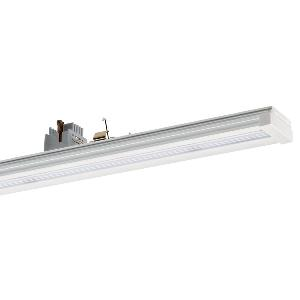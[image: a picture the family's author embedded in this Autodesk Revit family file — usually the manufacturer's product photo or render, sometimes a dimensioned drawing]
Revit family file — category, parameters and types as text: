
# Revit family: conveo_-_cvg_4500_840_w-p_ea_5_226848079-00804943_2f42
name_source: partatom
category: Lighting Fixtures
units: mm (PartAtom-declared; Revit-internal decimal feet)

## family parameters
Cut with Voids When Loaded = No
Host = Face
Light Source = No
Part Type = Normal
Room Calculation Point = No
Round Connector Dimension = Use Diameter
Shared = No

## types (1)
- CONVEO - CVG 4500/840/W-P/EA/5 (1 x LED, 4400 lm, 4000K)
    Apparent Load = 28 VA
    Approval mark = CE
    CIE Flux Codes = 54 85 97 100 100
    Color Rendering = 80-89
    Color Temperature = 4000K
    Control Gear = Electronic ballast
    Default Elevation = 1800 mm
    Description = CVG 4500/840/W-P/EA/5|Continuous-row system|light source: LED|work equipment: Electronic ballast|connected load: 220-240 V, 50-60 Hz|Power consumption: approx. 28 W|luminous flux: 4400 lm|luminous efficacy: 157 lm/W|colour temperature: Cold white, ca. 4000 K|color rendering index (CRI): >= 80|chromaticity tolerance:  3 SDCM|System of protection: IP 54|class of protection: I|technology: Switchable|luminaire body|material: Aluminium|surface: Powder coatet|colour: White|lamp cover: Acrylic (PMMA), Satine|weight (net): approx. 1.9 kg|Fastening: Available separately|minimum ambient temperature: -25 ░C|maximum ambient temperature: 56 ░C|glare control: Prism optics (linear)|Approval mark: VDE - ENEC|
    Frequency = 50 Hz
    Height = 70 mm
    Lamp = 1 x LED
    Lamp Light Flux = 4400 lm
    Lamp count = 1
    Length = 1500 mm
    Luminous efficacy = 157 lm/W
    Manufacturer = Waldmann
    ModVariant = No
    Model = 226848079-00804943
    Mounting Place = Ceiling
    Mounting Type = Pendant
    Number of Poles = 1
    OnlyDefault = Yes
    Power Factor = 1
    Product Name = CONVEO - CVG 4500/840/W-P/EA/5
    Product group = Continuous-row system (industry)
    ProductGroupID = 301
    Protection Class = Protection class I
    Protection Degree = IP 54
    RLX_Detail_Level = 1
    RlxData = <blob elided: 99029 chars, md5=05529012>
    Socket = socket
    Standby Power = 0 W
    System Light Flux = 4400 lm
    System Power = 28 W
    Type Comments = Product without accessories
    Type Image = 226848079-00804943-1p5.jpg
    URL = http://relux.com
    VarID = ---
    Voltage = 230 V
    Voltage Range = 220-240 V
    Weight = 0.00 kg
    Width = 64 mm

## geometry (parser evidence)
native form markers: Blend x4, Sweep x9
no freeform markers — native parametric forms only
